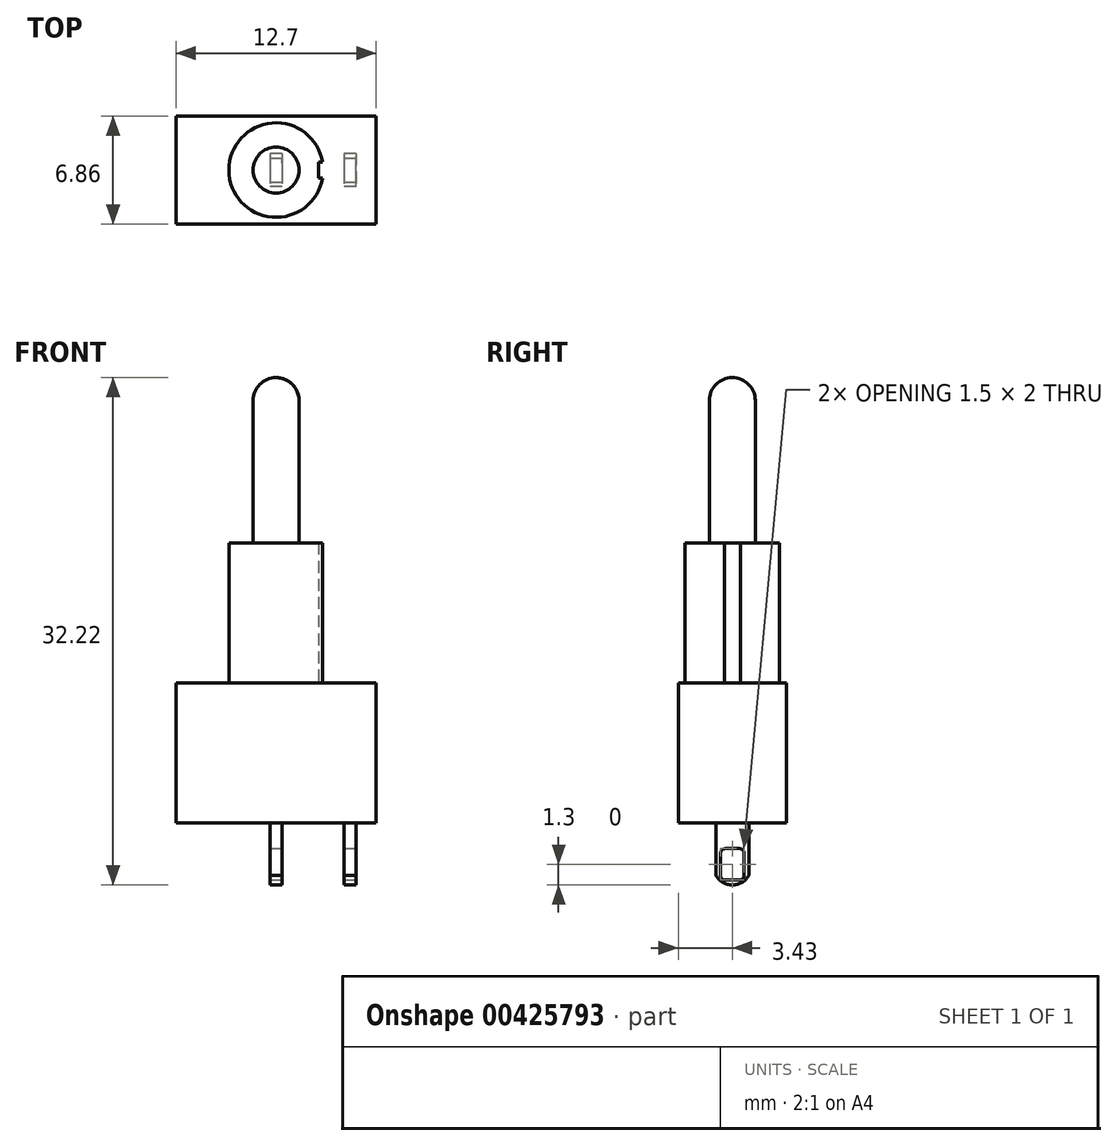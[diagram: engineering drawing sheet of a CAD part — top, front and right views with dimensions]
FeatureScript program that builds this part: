
annotation { "Feature Type Name" : "Feature", "Feature Type Description" : "" }
export const myFeature = defineFeature(function(context is Context, id is Id, definition is map)
    precondition{}
    {
        {
            var Q0;
            Q0=qCreatedBy(makeId("Top.planeOp"),FACE);
            var sketch = newSketch(context, id + "F0", { "sketchPlane" : qUnion([Q0])});
            skLineSegment(sketch, "E0.bottom", {"start": v(6.35, -3.43) * mm, "end": v(-6.35, -3.43) * mm});
            skLineSegment(sketch, "E0.top", {"start": v(6.35, 3.43) * mm, "end": v(-6.35, 3.43) * mm});
            skLineSegment(sketch, "E0.left", {"start": v(6.35, -3.43) * mm, "end": v(6.35, 3.43) * mm});
            skLineSegment(sketch, "E0.right", {"start": v(-6.35, -3.43) * mm, "end": v(-6.35, 3.43) * mm});
            skPoint(sketch, "E0.middle", {"position": v(0, 0) * mm});
            skSolve(sketch);
        }
        {
            var Q0;
            Q0 = qSketchRegion(id + "F0", true);
            extrude(context, id + "F1", {"entities" : qUnion([Q0]), "oppositeDirection" : true, "depth" : 8.9 * mm});
        }
        {
            var Q0;
            Q0=qCreatedBy(makeId("Top.planeOp"),FACE);
            var sketch = newSketch(context, id + "F2", { "sketchPlane" : qUnion([Q0])});
            skCircle(sketch, "E1", {"center": v(0, 0) * mm, "radius": 3 * mm});
            skSolve(sketch);
        }
        {
            var Q0;
            Q0 = qSketchRegion(id + "F2", true);
            extrude(context, id + "F3", {"entities" : qUnion([Q0]), "operationType" : NewBodyOperationType.ADD, "depth" : 8.9 * mm});
        }
        {
            var Q0;
            Q0=makeQuery(id+"F3.opExtrude","CAP_FACE",FACE,{"disambiguationData":[OSD([sQuery(id+"F2.wireOp",EDGE,"E1")])],"isStart":false});
            var sketch = newSketch(context, id + "F4", { "sketchPlane" : qUnion([Q0])});
            skCircle(sketch, "E2", {"center": v(0, 0) * mm, "radius": 1.46 * mm});
            skSolve(sketch);
        }
        {
            var Q0;
            Q0 = qSketchRegion(id + "F4", true);
            extrude(context, id + "F5", {"entities" : qUnion([Q0]), "operationType" : NewBodyOperationType.ADD, "depth" : 10.5 * mm});
        }
        {
            var Q0;
            Q0=makeQuery(id+"F5.opExtrude","CAP_FACE",FACE,{"disambiguationData":[OSD([sQuery(id+"F4.wireOp",EDGE,"E2")])],"isStart":false});
            fillet(context, id + "F6", {"entities" : qUnion([Q0]), "radius" : 1.46 * mm, "tangentPropagation" : true, "allowEdgeOverflow" : false});
        }
        {
            var Q0;
            Q0=qCreatedBy(makeId("Top.planeOp"),FACE);
            var sketch = newSketch(context, id + "F7", { "sketchPlane" : qUnion([Q0])});
            skLineSegment(sketch, "E3.bottom", {"start": v(3.12, -0.5) * mm, "end": v(2.68, -0.5) * mm});
            skLineSegment(sketch, "E3.top", {"start": v(3.12, 0.5) * mm, "end": v(2.68, 0.5) * mm});
            skLineSegment(sketch, "E3.left", {"start": v(3.12, -0.5) * mm, "end": v(3.12, 0.5) * mm});
            skLineSegment(sketch, "E3.right", {"start": v(2.68, -0.5) * mm, "end": v(2.68, 0.5) * mm});
            skPoint(sketch, "E3.middle", {"position": v(2.9, 0) * mm});
            skSolve(sketch);
        }
        {
            var Q0;
            Q0 = qSketchRegion(id + "F7", true);
            extrude(context, id + "F8", {"entities" : qUnion([Q0]), "operationType" : NewBodyOperationType.REMOVE, "depth" : 25 * mm});
        }
        {
            var Q0;
            Q0=makeQuery(id+"F1.opExtrude","CAP_FACE",FACE,{"disambiguationData":[OSD([sQuery(id+"F0.wireOp",EDGE,"E0.bottom"),sQuery(id+"F0.wireOp",EDGE,"E0.top"),sQuery(id+"F0.wireOp",EDGE,"E0.left"),sQuery(id+"F0.wireOp",EDGE,"E0.right")])],"isStart":false});
            var sketch = newSketch(context, id + "F9", { "sketchPlane" : qUnion([Q0])});
            skLineSegment(sketch, "E4.bottom", {"start": v(0.38, -1.05) * mm, "end": v(-0.38, -1.05) * mm});
            skLineSegment(sketch, "E4.top", {"start": v(0.38, 1.05) * mm, "end": v(-0.38, 1.05) * mm});
            skLineSegment(sketch, "E4.left", {"start": v(0.38, -1.05) * mm, "end": v(0.38, 1.05) * mm});
            skLineSegment(sketch, "E4.right", {"start": v(-0.38, -1.05) * mm, "end": v(-0.38, 1.05) * mm});
            skPoint(sketch, "E4.middle", {"position": v(0, 0) * mm});
            skLineSegment(sketch, "E5.bottom", {"start": v(5.08, -1.05) * mm, "end": v(4.32, -1.05) * mm});
            skLineSegment(sketch, "E5.top", {"start": v(5.08, 1.05) * mm, "end": v(4.32, 1.05) * mm});
            skLineSegment(sketch, "E5.left", {"start": v(5.08, -1.05) * mm, "end": v(5.08, 1.05) * mm});
            skLineSegment(sketch, "E5.right", {"start": v(4.32, -1.05) * mm, "end": v(4.32, 1.05) * mm});
            skPoint(sketch, "E5.middle", {"position": v(4.7, 0) * mm});
            skSolve(sketch);
        }
        {
            var Q0;
            Q0 = qSketchRegion(id + "F9", true);
            extrude(context, id + "F10", {"entities" : qUnion([Q0]), "operationType" : NewBodyOperationType.ADD, "depth" : (12.83 - 8.9) * mm});
        }
        {
            var Q0;
            Q0=makeQuery(id+"F10.opExtrude","SWEPT_FACE",FACE,{"disambiguationData":[OSD([sQuery(id+"F9.wireOp",EDGE,"E5.left")])]});
            var sketch = newSketch(context, id + "F11", { "sketchPlane" : qUnion([Q0])});
            skLineSegment(sketch, "E6.bottom", {"start": v(-0.45, -10.53) * mm, "end": v(0.45, -10.53) * mm});
            skLineSegment(sketch, "E6.top", {"start": v(-0.45, -12.53) * mm, "end": v(0.45, -12.53) * mm});
            skLineSegment(sketch, "E6.left", {"start": v(-0.75, -10.83) * mm, "end": v(-0.75, -12.23) * mm});
            skLineSegment(sketch, "E6.right", {"start": v(0.75, -10.83) * mm, "end": v(0.75, -12.23) * mm});
            skPoint(sketch, "E6.middle", {"position": v(0, -11.53) * mm});
            skPoint(sketch, "E6.middle.positionSnap0", {"position": v(0, -12.83) * mm});
            skPoint(sketch, "E6.centerSnap0", {"position": v(0, -12.83) * mm});
            skPoint(sketch, "E7.visualSharp", {"position": v(0.75, -12.53) * mm});
            skArc(sketch, "E7.filletArc", {"start": v(0.45, -12.53) * mm, "mid": v(0.66, -12.44) * mm, "end": v(0.75, -12.23) * mm});
            skPoint(sketch, "E8.visualSharp", {"position": v(-0.75, -12.53) * mm});
            skArc(sketch, "E8.filletArc", {"start": v(-0.75, -12.23) * mm, "mid": v(-0.66, -12.44) * mm, "end": v(-0.45, -12.53) * mm});
            skPoint(sketch, "E9.visualSharp", {"position": v(-0.75, -10.53) * mm});
            skArc(sketch, "E9.filletArc", {"start": v(-0.45, -10.53) * mm, "mid": v(-0.66, -10.62) * mm, "end": v(-0.75, -10.83) * mm});
            skPoint(sketch, "E10.visualSharp", {"position": v(0.75, -10.53) * mm});
            skArc(sketch, "E10.filletArc", {"start": v(0.75, -10.83) * mm, "mid": v(0.66, -10.62) * mm, "end": v(0.45, -10.53) * mm});
            skArc(sketch, "E11", {"start": v(-1.05, -12.23) * mm, "mid": v(0, -12.83) * mm, "end": v(1.05, -12.23) * mm});
            skSolve(sketch);
        }
        {
            var Q0;
            Q0=makeQuery(id+"F11.imprint","IMPRINT",FACE,{"disambiguationData":[TD([[makeQuery(id+"F11.imprint","IMPRINT",EDGE,{"derivedFrom":sQuery(id+"F11.wireOp",EDGE,"E6.bottom")}),-1.0]])]});
            var Q1;
            {var subQ0=sQuery(id+"F11.wireOp",EDGE,"E11");var subQ1=sQuery(id+"F9.wireOp",EDGE,"E5.left");var subQ4=makeQuery(id+"F10.opExtrude","CAP_EDGE",EDGE,{"disambiguationData":[OSD([subQ1])],"isStart":false});var subQ5=makeQuery(id+"F11.imprint","INTERSECT",VERTEX,{"derivedFrom":[subQ4,subQ0]});Q1=makeQuery(id+"F11.imprint","IMPRINT",FACE,{"disambiguationData":[TD([[makeQuery(id+"F11.imprint","IMPRINT",EDGE,{"disambiguationData":[TD([[subQ5,1.0]])],"derivedFrom":subQ0}),-1.0]])]});}
            var Q2;
            {var subQ0=sQuery(id+"F11.wireOp",EDGE,"E11");var subQ1=sQuery(id+"F9.wireOp",EDGE,"E5.left");var subQ4=makeQuery(id+"F10.opExtrude","CAP_EDGE",EDGE,{"disambiguationData":[OSD([subQ1])],"isStart":false});var subQ5=makeQuery(id+"F11.imprint","INTERSECT",VERTEX,{"derivedFrom":[subQ4,subQ0]});Q2=makeQuery(id+"F11.imprint","IMPRINT",FACE,{"disambiguationData":[TD([[makeQuery(id+"F11.imprint","IMPRINT",EDGE,{"disambiguationData":[TD([[subQ5,-1.0]])],"derivedFrom":subQ0}),-1.0]])]});}
            extrude(context, id + "F12", {"entities" : qUnion([Q0, Q1, Q2]), "operationType" : NewBodyOperationType.REMOVE, "endBound" : BoundingType.THROUGH_ALL, "oppositeDirection" : true, "depth" : 25 * mm});
        }
    });
